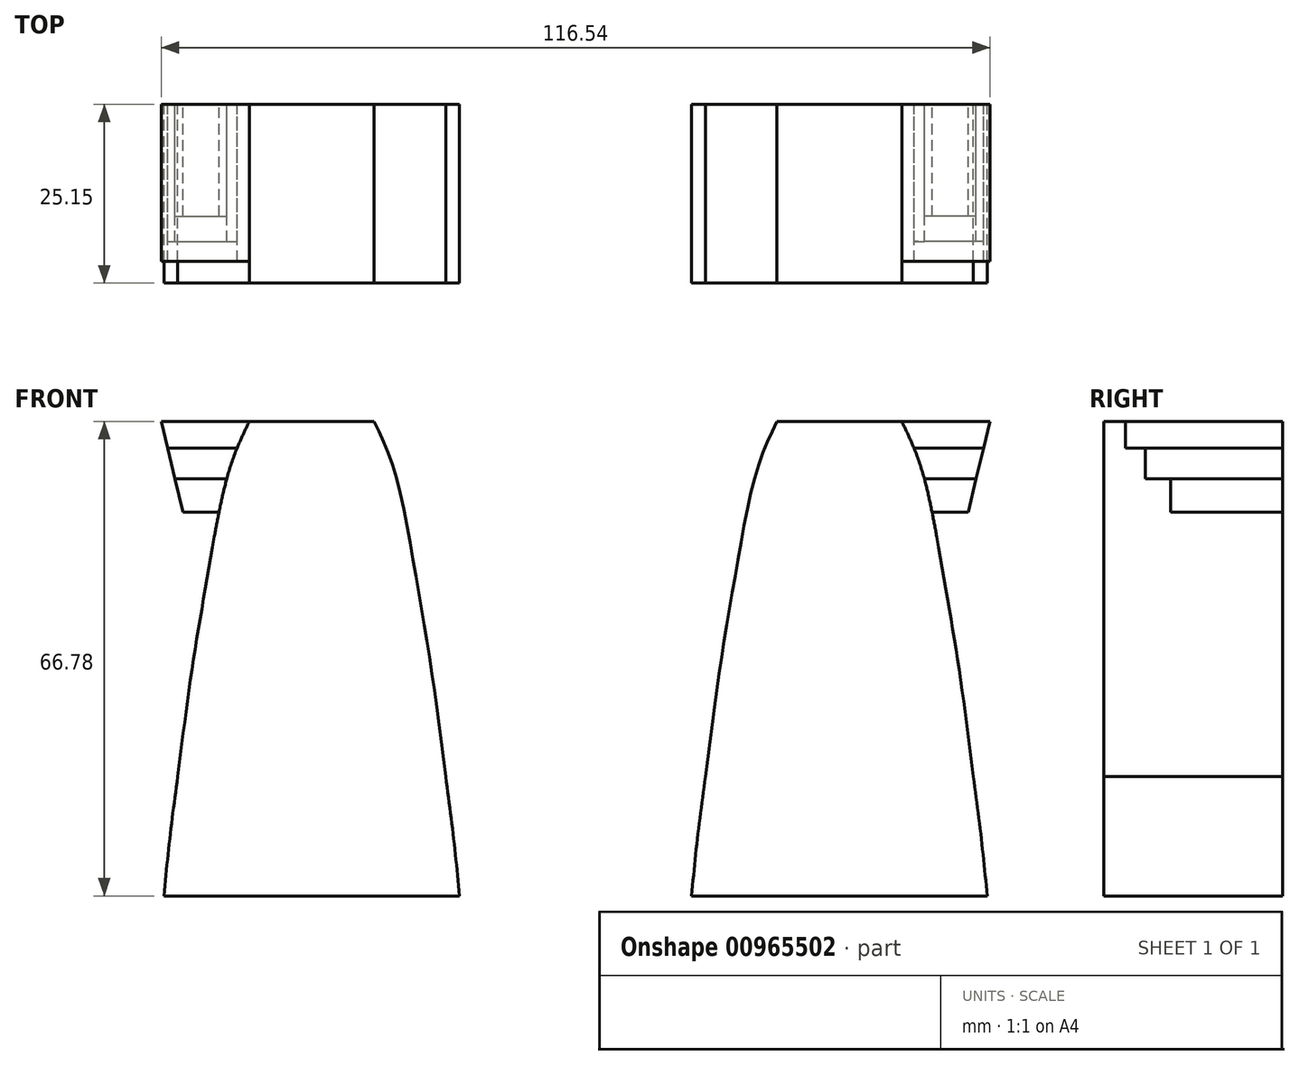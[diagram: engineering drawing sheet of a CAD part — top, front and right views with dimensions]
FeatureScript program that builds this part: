
annotation { "Feature Type Name" : "Feature", "Feature Type Description" : "" }
export const myFeature = defineFeature(function(context is Context, id is Id, definition is map)
    precondition{}
    {
        {
            var Q0;
            Q0=qCreatedBy(makeId("Front.planeOp"),FACE);
            var sketch = newSketch(context, id + "F0", { "sketchPlane" : qUnion([Q0])});
            skFitSpline(sketch, "E0", {"points": [v(-55.94, -50) * mm, v(-53.88, -34.52) * mm, v(-51.55, -20.58) * mm, v(-48.72, -6.9) * mm, v(-45.88, 0) * mm], "startDerivative": vector(7.1, 56.67) * mm, "endDerivative": vector(15.54, 32.16) * mm});
            skFitSpline(sketch, "E1.MirrorCS", {"points": [v(-18.26, -50) * mm, v(-20.33, -34.52) * mm, v(-22.65, -20.58) * mm, v(-25.49, -6.9) * mm, v(-28.33, 0) * mm], "startDerivative": vector(-7.1, 56.67) * mm, "endDerivative": vector(-15.54, 32.16) * mm});
            skLineSegment(sketch, "E2", {"start": v(-45.88, 0) * mm, "end": v(-28.33, 0) * mm});
            skLineSegment(sketch, "E3", {"start": v(-45.88, 0) * mm, "end": v(-58.27, 0) * mm});
            skLineSegment(sketch, "E4", {"start": v(-58.27, 0) * mm, "end": v(-54.4, -16.2) * mm});
            skLineSegment(sketch, "E5", {"start": v(-54.4, -16.2) * mm, "end": v(-50.79, -16.2) * mm});
            skLineSegment(sketch, "E6", {"start": v(-55.2, -12.79) * mm, "end": v(-50.14, -12.79) * mm});
            skLineSegment(sketch, "E7", {"start": v(-56.33, -8.1) * mm, "end": v(-49.06, -8.1) * mm});
            skLineSegment(sketch, "E8", {"start": v(-57.37, -3.74) * mm, "end": v(-47.59, -3.74) * mm});
            skFitSpline(sketch, "E9.MirrorCS", {"points": [v(18.26, -50) * mm, v(20.33, -34.52) * mm, v(22.65, -20.58) * mm, v(25.49, -6.9) * mm, v(28.33, 0) * mm], "startDerivative": vector(7.1, 56.67) * mm, "endDerivative": vector(15.54, 32.16) * mm});
            skFitSpline(sketch, "E10.MirrorCS", {"points": [v(55.94, -50) * mm, v(53.88, -34.52) * mm, v(51.55, -20.58) * mm, v(48.72, -6.9) * mm, v(45.88, 0) * mm], "startDerivative": vector(-7.1, 56.67) * mm, "endDerivative": vector(-15.54, 32.16) * mm});
            skLineSegment(sketch, "E11.MirrorCS", {"start": v(45.88, 0) * mm, "end": v(28.33, 0) * mm});
            skLineSegment(sketch, "E12.MirrorCS", {"start": v(58.27, 0) * mm, "end": v(54.4, -16.2) * mm});
            skLineSegment(sketch, "E13.MirrorCS", {"start": v(55.2, -12.79) * mm, "end": v(50.14, -12.79) * mm});
            skLineSegment(sketch, "E14.MirrorCS", {"start": v(57.37, -3.74) * mm, "end": v(47.59, -3.74) * mm});
            skLineSegment(sketch, "E15.MirrorCS", {"start": v(56.33, -8.1) * mm, "end": v(49.06, -8.1) * mm});
            skLineSegment(sketch, "E16.MirrorCS", {"start": v(54.4, -16.2) * mm, "end": v(50.79, -16.2) * mm});
            skLineSegment(sketch, "E17.MirrorCS", {"start": v(45.88, 0) * mm, "end": v(58.27, 0) * mm});
            skFitSpline(sketch, "E18", {"points": [v(-55.94, -50) * mm, v(-57.03, -58.38) * mm, v(-57.9, -66.78) * mm], "startDerivative": vector(-2.27, -16.7) * mm, "endDerivative": vector(-1.62, -16.6) * mm});
            skLineSegment(sketch, "E19", {"start": v(-37.1, -66.78) * mm, "end": v(-57.9, -66.78) * mm});
            skFitSpline(sketch, "E20.MirrorCS", {"points": [v(-18.26, -50) * mm, v(-17.18, -58.38) * mm, v(-16.31, -66.78) * mm], "startDerivative": vector(2.27, -16.7) * mm, "endDerivative": vector(1.62, -16.6) * mm});
            skLineSegment(sketch, "E21.MirrorCS", {"start": v(-37.1, -66.78) * mm, "end": v(-16.31, -66.78) * mm});
            skFitSpline(sketch, "E22.MirrorCS", {"points": [v(18.26, -50) * mm, v(17.18, -58.38) * mm, v(16.31, -66.78) * mm], "startDerivative": vector(-2.27, -16.7) * mm, "endDerivative": vector(-1.62, -16.6) * mm});
            skFitSpline(sketch, "E23.MirrorCS", {"points": [v(55.94, -50) * mm, v(57.03, -58.38) * mm, v(57.9, -66.78) * mm], "startDerivative": vector(2.27, -16.7) * mm, "endDerivative": vector(1.62, -16.6) * mm});
            skLineSegment(sketch, "E24.MirrorCS", {"start": v(37.1, -66.78) * mm, "end": v(57.9, -66.78) * mm});
            skLineSegment(sketch, "E25.MirrorCS", {"start": v(37.1, -66.78) * mm, "end": v(16.31, -66.78) * mm});
            skSolve(sketch);
        }
        {
            var Q0;
            {var subQ4=sQuery(id+"F0.wireOp",EDGE,"P61KTGQD-8SEu-a95N-QXux-OcNOB74UNl6T");Q0=makeQuery(id+"F0.imprint","IMPRINT",FACE,{"disambiguationData":[TD([[makeQuery(id+"F0.imprint","IMPRINT",EDGE,{"derivedFrom":subQ4}),1.0]])]});}
            var Q1;
            Q1=makeQuery(id+"F0.imprint","IMPRINT",FACE,{"disambiguationData":[TD([[makeQuery(id+"F0.imprint","IMPRINT",EDGE,{"derivedFrom":sQuery(id+"F0.wireOp",EDGE,"E9.MirrorCS")}),-1.0]])]});
            var Q2;
            Q2=makeQuery(id+"F0.imprint","IMPRINT",FACE,{"disambiguationData":[TD([[makeQuery(id+"F0.imprint","IMPRINT",EDGE,{"derivedFrom":sQuery(id+"F0.wireOp",EDGE,"E1.MirrorCS")}),1.0]])]});
            extrude(context, id + "F1", {"entities" : qUnion([Q0, Q1, Q2]), "depth" : 25.15 * mm, "offsetDistance" : 25.4 * mm});
        }
        {
            var Q0;
            {var subQ2=sQuery(id+"F0.wireOp",EDGE,"E14.MirrorCS");Q0=makeQuery(id+"F0.imprint","IMPRINT",FACE,{"disambiguationData":[TD([[makeQuery(id+"F0.imprint","IMPRINT",EDGE,{"derivedFrom":subQ2}),-1.0]])]});}
            var Q1;
            {var subQ0=sQuery(id+"F0.wireOp",EDGE,"E3");Q1=makeQuery(id+"F0.imprint","IMPRINT",FACE,{"disambiguationData":[TD([[makeQuery(id+"F0.imprint","IMPRINT",EDGE,{"derivedFrom":subQ0}),1.0]])]});}
            extrude(context, id + "F2", {"entities" : qUnion([Q0, Q1]), "depth" : 22.1 * mm, "offsetDistance" : 25.4 * mm});
        }
        {
            var Q0;
            {var subQ0=sQuery(id+"F0.wireOp",EDGE,"E14.MirrorCS");Q0=makeQuery(id+"F0.imprint","IMPRINT",FACE,{"disambiguationData":[TD([[makeQuery(id+"F0.imprint","IMPRINT",EDGE,{"derivedFrom":subQ0}),1.0]])]});}
            var Q1;
            {var subQ0=sQuery(id+"F0.wireOp",EDGE,"E7");Q1=makeQuery(id+"F0.imprint","IMPRINT",FACE,{"disambiguationData":[TD([[makeQuery(id+"F0.imprint","IMPRINT",EDGE,{"derivedFrom":subQ0}),1.0]])]});}
            extrude(context, id + "F3", {"entities" : qUnion([Q0, Q1]), "depth" : 19.3 * mm, "offsetDistance" : 25.4 * mm});
        }
        {
            var Q0;
            {var subQ0=sQuery(id+"F0.wireOp",EDGE,"E6");Q0=makeQuery(id+"F0.imprint","IMPRINT",FACE,{"disambiguationData":[TD([[makeQuery(id+"F0.imprint","IMPRINT",EDGE,{"derivedFrom":subQ0}),1.0]])]});}
            var Q1;
            {var subQ0=sQuery(id+"F0.wireOp",EDGE,"E13.MirrorCS");Q1=makeQuery(id+"F0.imprint","IMPRINT",FACE,{"disambiguationData":[TD([[makeQuery(id+"F0.imprint","IMPRINT",EDGE,{"derivedFrom":subQ0}),-1.0]])]});}
            extrude(context, id + "F4", {"entities" : qUnion([Q0, Q1]), "depth" : 15.75 * mm, "offsetDistance" : 25.4 * mm});
        }
    });
